# Revit family: STL22417BR_30_STL22417PTO_30
name_source: partatom
category: Luminárias
units: mm (PartAtom-declared; Revit-internal decimal feet)

## family parameters
Com base no plano de trabalho = Não
Compartilhado = Não
Corte com vazios quando carregada = Não
Cota do conector redondo = Utilizar diâmetro
Fonte luminosa = Sim
Manter orientação da anotação = Não
Número OmniClass = 23.80.70.00
Ponto de cálculo do ambiente = Não
Sempre na vertical = Sim
Tipo de parte = Normal
Título OmniClass = Lighting

## types (2) — shared parameters
Acabamento Spot = Al - Preto
Dimerização = Não dimerizável
Fabricante = Stella
Filtro de cor = 16777215
Fluxo Luminoso = 700 lm
Grau de proteção (IP) = IP20
IRC (Índice de reprodução de cores) = >93 (R9>60)
Lente = Vidro
Luminoso = Luminoso - 3000K
Modelo = Trace - Spot c/ LED Integrado
Potência máxima = 7 W
Temperatura da cor (K) = 3000 K
Tensão Elétrica = 100V/240V
Troca de temperatura da cor de lâmpada com esmaecimento = <Nenhum>
URL = https://stella.com.br
Ângulo de Abertura = 34°
Ângulo de inclinação = 180.00°
zero-valued in all types: Altura do Spot, Comprimento do Spot, Diâmetro do Spot, Elevação padrão

## per-type parameters (varying)
| type | Arquivo de rede fotométrica | Estrutura | Referência |
| STL22417PTO/30 - BIVOLT - 3000K - 700lm - 34° | STELLA - STL22417PTO-30 - TRACE 7W - SPOT COM LED INTEGRADO.ies | Al - Preto | STL22417PTO/30 |
| STL22417BR/30 - BIVOLT - 3000K - 700lm - 34° | STELLA - STL22417BR-30 - TRACE 7W - SPOT COM LED INTEGRADO.ies | Al - Branco | STL22417BR/30 |
